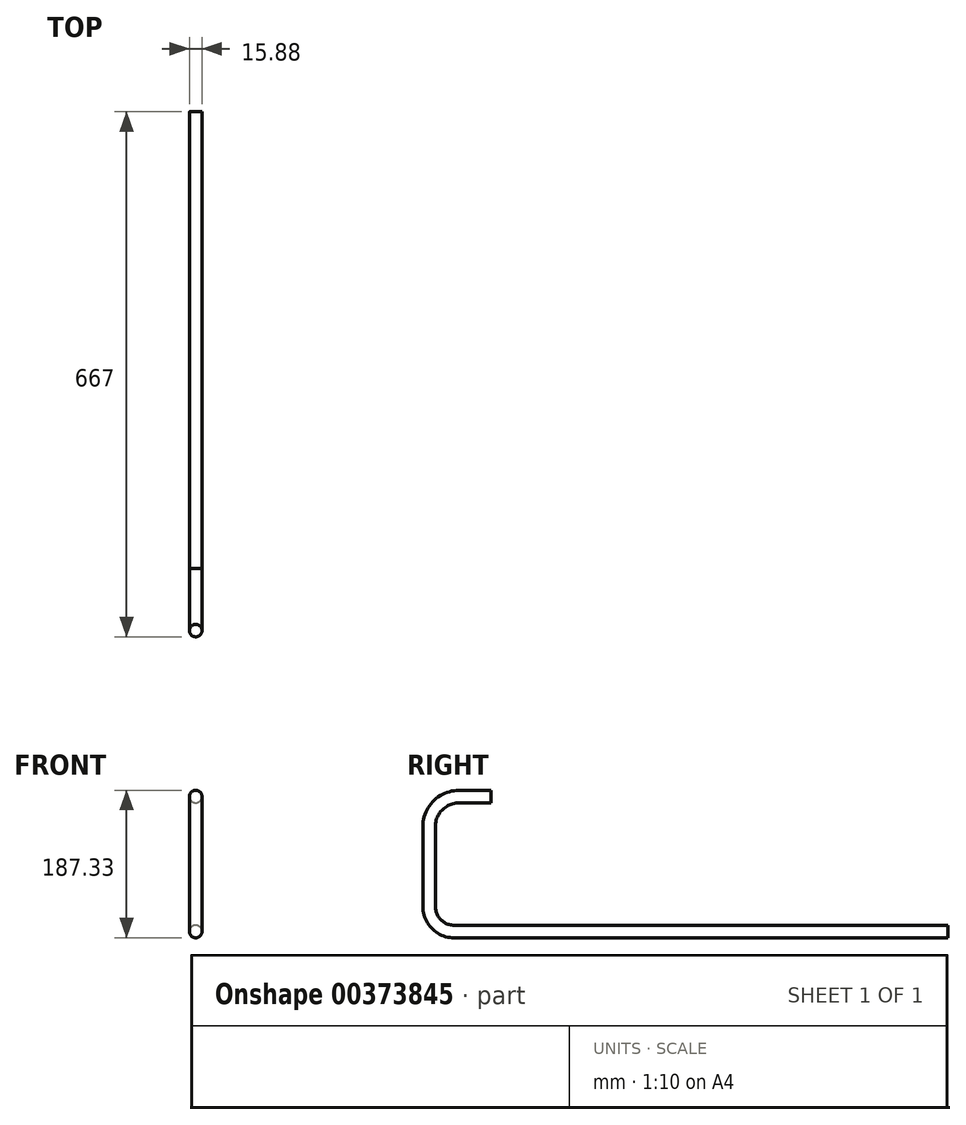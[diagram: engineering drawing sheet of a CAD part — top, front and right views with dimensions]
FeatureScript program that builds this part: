
annotation { "Feature Type Name" : "Feature", "Feature Type Description" : "" }
export const myFeature = defineFeature(function(context is Context, id is Id, definition is map)
    precondition{}
    {
        {
            var Q0;
            Q0=qCreatedBy(makeId("Front.planeOp"),FACE);
            var sketch = newSketch(context, id + "F0", { "sketchPlane" : qUnion([Q0])});
            skCircle(sketch, "E0", {"center": v(0, 0) * mm, "radius": 7.94 * mm});
            skSolve(sketch);
        }
        {
            var Q0;
            Q0=qCreatedBy(makeId("Right.planeOp"),FACE);
            var sketch = newSketch(context, id + "F1", { "sketchPlane" : qUnion([Q0])});
            skLineSegment(sketch, "E1", {"start": v(0, 0) * mm, "end": v(-40.73, 0) * mm});
            skLineSegment(sketch, "E2", {"start": v(-78.83, -38.1) * mm, "end": v(-78.83, -139.7) * mm});
            skLineSegment(sketch, "E3", {"start": v(-47.08, -171.45) * mm, "end": v(580.24, -171.45) * mm});
            skPoint(sketch, "E4.visualSharp", {"position": v(-78.83, 0) * mm});
            skArc(sketch, "E4.filletArc", {"start": v(-40.73, 0) * mm, "mid": v(-67.67, -11.16) * mm, "end": v(-78.83, -38.1) * mm});
            skPoint(sketch, "E5.visualSharp", {"position": v(-78.83, -171.45) * mm});
            skArc(sketch, "E5.filletArc", {"start": v(-78.83, -139.7) * mm, "mid": v(-69.53, -162.15) * mm, "end": v(-47.08, -171.45) * mm});
            skSolve(sketch);
        }
        {
            var Q0;
            Q0 = qSketchRegion(id + "F0", true);
            var Q1;
            Q1 = qConstructionFilter(qBodyType(qCreatedBy(id + "F1" ,EDGE), BodyType.WIRE), ConstructionObject.NO);
            sweep(context, id + "F2", {"profiles" : qUnion([Q0]), "path" : qUnion([Q1])});
        }
    });
